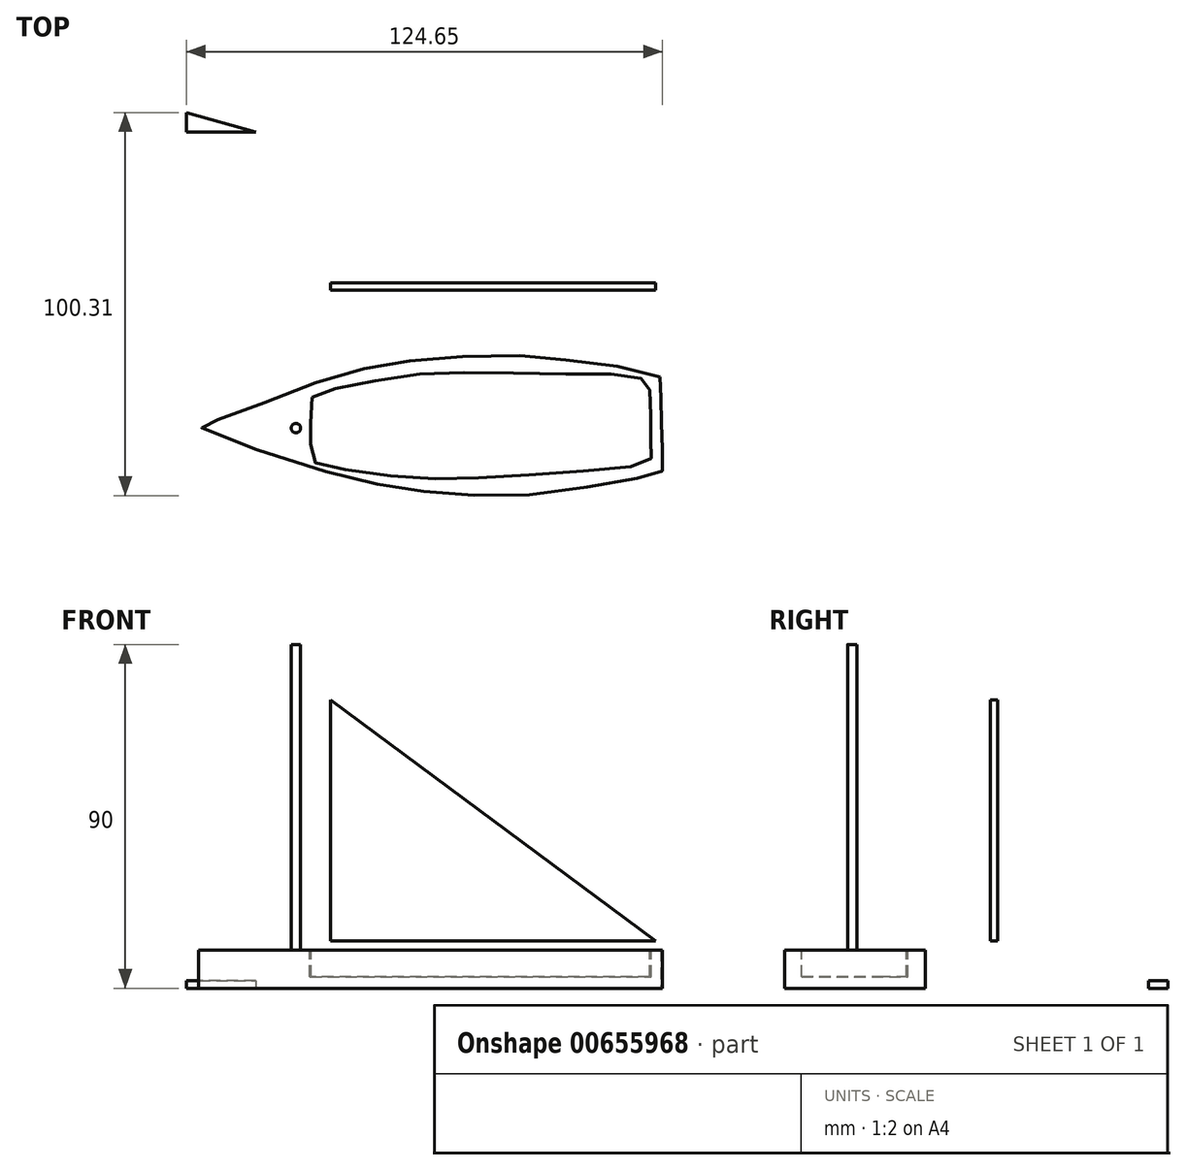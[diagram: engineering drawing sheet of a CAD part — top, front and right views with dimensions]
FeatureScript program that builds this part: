
annotation { "Feature Type Name" : "Feature", "Feature Type Description" : "" }
export const myFeature = defineFeature(function(context is Context, id is Id, definition is map)
    precondition{}
    {
        {
            var Q0;
            Q0=qCreatedBy(makeId("Top.planeOp"),FACE);
            var sketch = newSketch(context, id + "F0", { "sketchPlane" : qUnion([Q0])});
            skPoint(sketch, "E0.7.internal.snap0", {"position": v(74.71, -37.28) * mm});
            skPoint(sketch, "E0.16.internal.snap0", {"position": v(74.71, -37.28) * mm});
            skFitSpline(sketch, "E0", {"points": [v(62.17, -24.63) * mm, v(44.5, -21.12) * mm, v(27.8, -19.14) * mm, v(2.75, -19.8) * mm, v(-14.64, -22.4) * mm, v(-34.68, -28.69) * mm, v(-54.02, -35.94) * mm, v(-58.53, -37.28) * mm, v(-32.36, -47.3) * mm, v(-8.98, -53.28) * mm, v(9.5, -55.38) * mm, v(33.5, -55.07) * mm, v(56.1, -51.27) * mm, v(62.48, -49.89) * mm, v(62.76, -46.97) * mm, v(62.76, -42.66) * mm, v(62.63, -37.28) * mm, v(62.5, -32.08) * mm, v(62.5, -27.5) * mm, v(62.17, -24.63) * mm]});
            skSolve(sketch);
        }
        {
            var Q0;
            Q0=makeQuery(id+"F0.imprint","IMPRINT",FACE,{"disambiguationData":[TD([[makeQuery(id+"F0.imprint","IMPRINT",EDGE,{"derivedFrom":sQuery(id+"F0.wireOp",EDGE,"E0")}),1.0]])]});
            var sketch = newSketch(context, id + "F1", { "sketchPlane" : qUnion([Q0])});
            skFitSpline(sketch, "E1", {"points": [v(-28.87, -29.94) * mm, v(-29.24, -37) * mm, v(-29.22, -41.44) * mm, v(-28.93, -46.14) * mm, v(-24.4, -48.2) * mm, v(-4.6, -50.97) * mm, v(14.93, -51.13) * mm, v(43.27, -49.2) * mm, v(59.12, -47.02) * mm, v(59.9, -45.26) * mm, v(59.76, -41.2) * mm, v(59.74, -35.92) * mm, v(59.48, -28.35) * mm, v(59.36, -26.81) * mm, v(56.34, -24.74) * mm, v(42.94, -23.96) * mm, v(15.8, -23.56) * mm, v(-4.98, -24.44) * mm, v(-23.28, -27.84) * mm, v(-28.87, -29.94) * mm]});
            skSolve(sketch);
        }
        {
            var Q0;
            Q0=makeQuery(id+"F1.imprint","IMPRINT",FACE,{"disambiguationData":[TD([[makeQuery(id+"F1.imprint","IMPRINT",EDGE,{"derivedFrom":sQuery(id+"F1.wireOp",EDGE,"E1")}),-1.0]])]});
            extrude(context, id + "F2", {"entities" : qUnion([Q0]), "depth" : 10 * mm, "offsetDistance" : 25 * mm});
        }
        {
            var Q0;
            Q0 = qSketchRegion(id + "F1", true);
            var Q1;
            Q1=makeQuery(id+"F0.imprint","IMPRINT",FACE,{"disambiguationData":[TD([[makeQuery(id+"F0.imprint","IMPRINT",EDGE,{"derivedFrom":sQuery(id+"F0.wireOp",EDGE,"E0")}),1.0]])]});
            extrude(context, id + "F3", {"entities" : qUnion([Q0, Q1]), "operationType" : NewBodyOperationType.ADD, "depth" : 3 * mm, "offsetDistance" : 25 * mm});
        }
        {
            var Q0;
            Q0=makeQuery(id+"F2.opExtrude","CAP_FACE",FACE,{"disambiguationData":[OSD([sQuery(id+"F0.wireOp",EDGE,"E0"),sQuery(id+"F1.wireOp",EDGE,"E1")])],"isStart":false});
            var sketch = newSketch(context, id + "F4", { "sketchPlane" : qUnion([Q0])});
            skCircle(sketch, "E2", {"center": v(-33.12, -38.07) * mm, "radius": 1.23 * mm});
            skSolve(sketch);
        }
        {
            var Q0;
            Q0 = qSketchRegion(id + "F4", true);
            extrude(context, id + "F5", {"entities" : qUnion([Q0]), "operationType" : NewBodyOperationType.ADD, "depth" : 80 * mm, "offsetDistance" : 25 * mm});
        }
        {
            var Q0;
            Q0=qCreatedBy(makeId("Top.planeOp"),FACE);
            var sketch = newSketch(context, id + "F6", { "sketchPlane" : qUnion([Q0])});
            skLineSegment(sketch, "E3", {"start": v(-30.29, 0) * mm, "end": v(-30.29, 63.37) * mm});
            skLineSegment(sketch, "E4", {"start": v(-30.29, 63.37) * mm, "end": v(41.78, 0) * mm});
            skLineSegment(sketch, "E5", {"start": v(41.78, 0) * mm, "end": v(-30.29, 0) * mm});
            skSolve(sketch);
        }
        {
            var Q0;
            Q0 = qSketchRegion(id + "F6", true);
            extrude(context, id + "F7", {"entities" : qUnion([Q0]), "depth" : 2 * mm, "offsetDistance" : 25 * mm});
        }
        {
            var Q0;
            Q0=makeQuery(id+"F7.opExtrude","SWEPT_BODY",BODY,{"disambiguationData":[OSD([sQuery(id+"F6.wireOp",EDGE,"E3"),sQuery(id+"F6.wireOp",EDGE,"E4"),sQuery(id+"F6.wireOp",EDGE,"E5")])]});
            deleteBodies(context, id + "F8", {"entities" : qUnion([Q0])});
        }
        {
            var Q0;
            Q0=qCreatedBy(makeId("Front.planeOp"),FACE);
            var sketch = newSketch(context, id + "F9", { "sketchPlane" : qUnion([Q0])});
            skLineSegment(sketch, "E6", {"start": v(-24.11, 75.46) * mm, "end": v(-24.11, 12.38) * mm});
            skLineSegment(sketch, "E7", {"start": v(-24.11, 12.38) * mm, "end": v(61.08, 12.38) * mm});
            skLineSegment(sketch, "E8", {"start": v(61.08, 12.38) * mm, "end": v(-24.11, 75.46) * mm});
            skSolve(sketch);
        }
        {
            var Q0;
            Q0 = qSketchRegion(id + "F9", true);
            extrude(context, id + "F10", {"entities" : qUnion([Q0]), "depth" : 2 * mm, "offsetDistance" : 25 * mm});
        }
        {
            var Q0;
            Q0=qCreatedBy(makeId("Top.planeOp"),FACE);
            var sketch = newSketch(context, id + "F11", { "sketchPlane" : qUnion([Q0])});
            skLineSegment(sketch, "E9", {"start": v(-61.8, 44.54) * mm, "end": v(-61.8, 39.47) * mm});
            skLineSegment(sketch, "E10", {"start": v(-61.8, 39.47) * mm, "end": v(-43.68, 39.47) * mm});
            skLineSegment(sketch, "E11", {"start": v(-43.68, 39.47) * mm, "end": v(-61.8, 44.54) * mm});
            skSolve(sketch);
        }
        {
            var Q0;
            Q0 = qSketchRegion(id + "F11", true);
            extrude(context, id + "F12", {"entities" : qUnion([Q0]), "depth" : 2 * mm, "offsetDistance" : 25 * mm});
        }
    });
